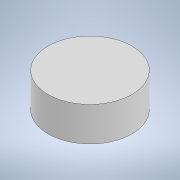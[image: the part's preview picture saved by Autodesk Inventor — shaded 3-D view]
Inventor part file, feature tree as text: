
AUTODESK INVENTOR PART (.ipt)
format: ipt  version: 2020.3 (Build 243373000, 373)  size: 88,064 bytes
history: native  units: mm
features: extrude x1, sketch x1
ambient origin geometry x8: Origin, YZ Plane, XZ Plane, XY Plane, X Axis, Y Axis, Z Axis, Center Point
bodies: Solid1 (feature_tree)
feature tree (2):
  extrude  "Extrusion1"  Depth=20.0mm TaperAngle=0.0deg
  sketch  "Sketch1"  dims[d0=49.0mm d1=20.0mm d2=0.0mm]
